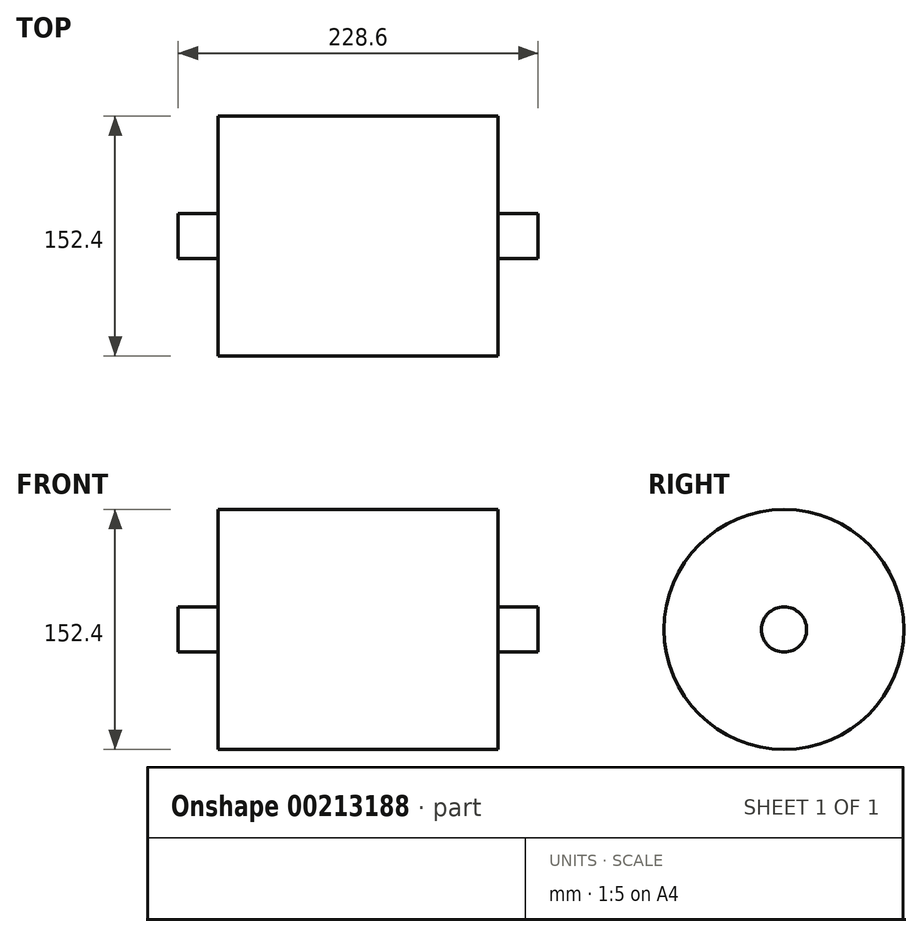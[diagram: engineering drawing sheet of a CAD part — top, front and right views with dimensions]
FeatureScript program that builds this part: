
annotation { "Feature Type Name" : "Feature", "Feature Type Description" : "" }
export const myFeature = defineFeature(function(context is Context, id is Id, definition is map)
    precondition{}
    {
        {
            var Q0;
            Q0=qCreatedBy(makeId("Right.planeOp"),FACE);
            var sketch = newSketch(context, id + "F0", { "sketchPlane" : qUnion([Q0])});
            skCircle(sketch, "E0", {"center": v(0, 0) * mm, "radius": 76.2 * mm});
            skSolve(sketch);
        }
        {
            var Q0;
            Q0=makeQuery(id+"F0.imprint","IMPRINT",FACE,{"disambiguationData":[TD([[makeQuery(id+"F0.imprint","IMPRINT",EDGE,{"derivedFrom":sQuery(id+"F0.wireOp",EDGE,"E0")}),1.0]])]});
            var Q1;
            Q1=sQuery(id+"F0.wireOp",EDGE,"E0");
            extrude(context, id + "F1", {"entities" : qUnion([Q0]), "surfaceEntities" : qUnion([Q1]), "endBound" : BoundingType.SYMMETRIC, "depth" : 177.8 * mm});
        }
        {
            var Q0;
            Q0=makeQuery(id+"F1.opExtrude","CAP_FACE",FACE,{"disambiguationData":[OSD([sQuery(id+"F0.wireOp",EDGE,"E0")])],"isStart":false});
            var sketch = newSketch(context, id + "F2", { "sketchPlane" : qUnion([Q0])});
            skCircle(sketch, "E1", {"center": v(0, 0) * mm, "radius": 14.36 * mm});
            skSolve(sketch);
        }
        {
            var Q0;
            Q0=makeQuery(id+"F2.imprint","IMPRINT",FACE,{"disambiguationData":[TD([[makeQuery(id+"F2.imprint","IMPRINT",EDGE,{"derivedFrom":sQuery(id+"F2.wireOp",EDGE,"E1")}),1.0]])]});
            extrude(context, id + "F3", {"entities" : qUnion([Q0]), "operationType" : NewBodyOperationType.ADD, "depth" : 25.4 * mm});
        }
        {
            var Q0;
            Q0=makeQuery(id+"F1.opExtrude","SWEPT_BODY",BODY,{"disambiguationData":[OSD([sQuery(id+"F0.wireOp",EDGE,"E0")])]});
            var Q1;
            Q1=qCreatedBy(makeId("Right.planeOp"),FACE);
            mirror(context, id + "F4", {"operationType" : NewBodyOperationType.ADD, "entities" : qUnion([Q0]), "mirrorPlane" : qUnion([Q1])});
        }
    });
